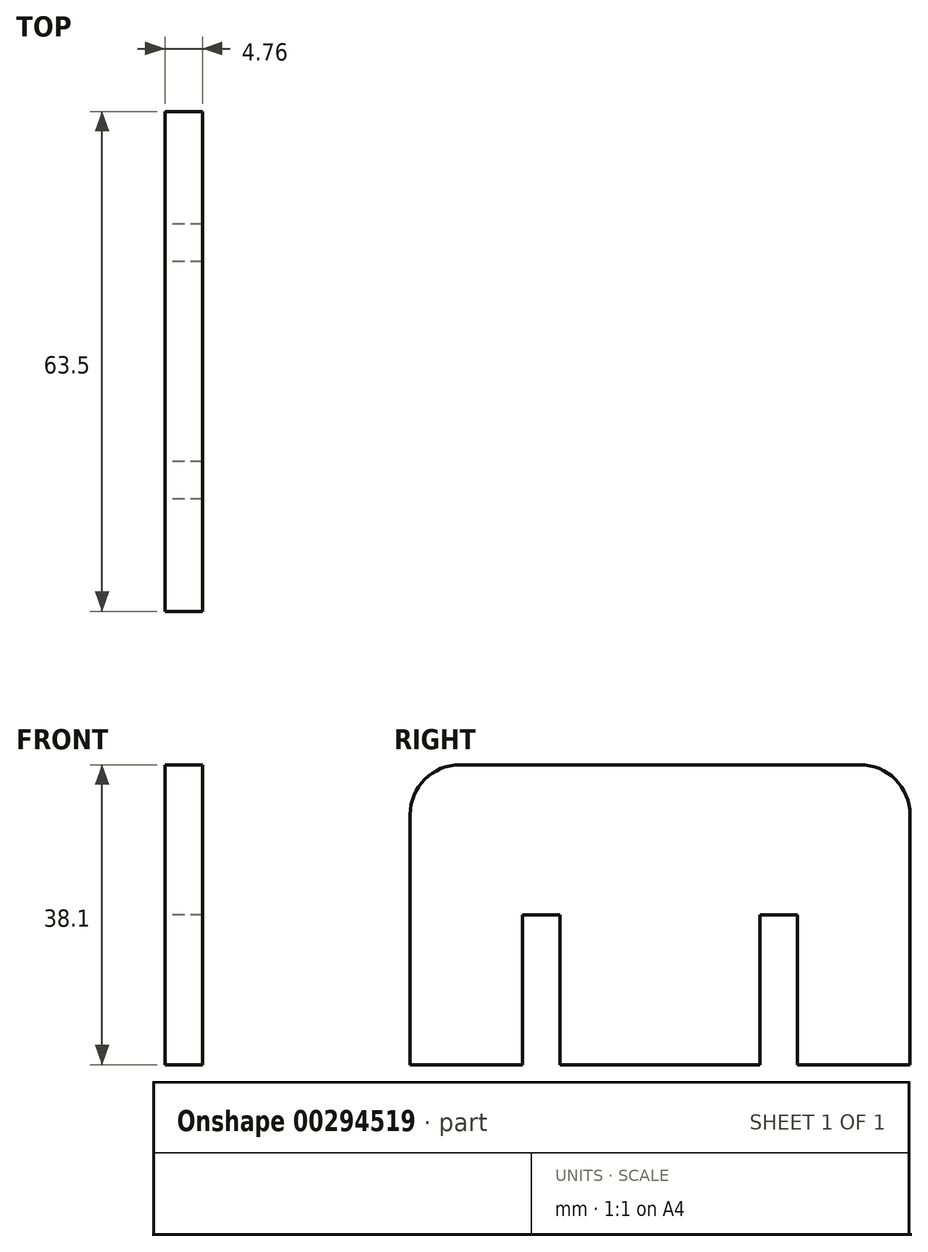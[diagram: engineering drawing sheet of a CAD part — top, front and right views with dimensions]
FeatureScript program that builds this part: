
annotation { "Feature Type Name" : "Feature", "Feature Type Description" : "" }
export const myFeature = defineFeature(function(context is Context, id is Id, definition is map)
    precondition{}
    {
        {
            var Q0;
            Q0=qCreatedBy(makeId("Right.planeOp"),FACE);
            var sketch = newSketch(context, id + "F0", { "sketchPlane" : qUnion([Q0])});
            skLineSegment(sketch, "E0.bottom", {"start": v(0, 0) * mm, "end": v(14.29, 0) * mm});
            skLineSegment(sketch, "E0.top", {"start": v(6.35, 38.1) * mm, "end": v(57.15, 38.1) * mm});
            skLineSegment(sketch, "E0.left", {"start": v(0, 0) * mm, "end": v(0, 31.75) * mm});
            skLineSegment(sketch, "E0.right", {"start": v(63.5, 0) * mm, "end": v(63.5, 31.75) * mm});
            skPoint(sketch, "E1.visualSharp", {"position": v(0, 38.1) * mm});
            skArc(sketch, "E1.filletArc", {"start": v(6.35, 38.1) * mm, "mid": v(1.86, 36.24) * mm, "end": v(0, 31.75) * mm});
            skPoint(sketch, "E2.visualSharp", {"position": v(63.5, 38.1) * mm});
            skArc(sketch, "E2.filletArc", {"start": v(63.5, 31.75) * mm, "mid": v(61.64, 36.24) * mm, "end": v(57.15, 38.1) * mm});
            skLineSegment(sketch, "E3", {"start": v(31.75, 38.1) * mm, "end": v(31.75, 0) * mm, "construction": true});
            skPoint(sketch, "E4.oppositeSnap0", {"position": v(31.75, 19.05) * mm});
            skLineSegment(sketch, "E4.top", {"start": v(44.45, 19.05) * mm, "end": v(49.21, 19.05) * mm});
            skLineSegment(sketch, "E4.left", {"start": v(44.45, 0) * mm, "end": v(44.45, 19.05) * mm});
            skLineSegment(sketch, "E4.right", {"start": v(49.21, 0) * mm, "end": v(49.21, 19.05) * mm});
            skLineSegment(sketch, "E5.MirrorCS", {"start": v(19.05, 19.05) * mm, "end": v(14.29, 19.05) * mm});
            skLineSegment(sketch, "E6.MirrorCS", {"start": v(14.29, 0) * mm, "end": v(14.29, 19.05) * mm});
            skLineSegment(sketch, "E7.MirrorCS", {"start": v(19.05, 0) * mm, "end": v(19.05, 19.05) * mm});
            skLineSegment(sketch, "E8.trimOffspring", {"start": v(19.05, 0) * mm, "end": v(44.45, 0) * mm});
            skLineSegment(sketch, "E9.trimOffspring", {"start": v(49.21, 0) * mm, "end": v(63.5, 0) * mm});
            skSolve(sketch);
        }
        {
            var Q0;
            Q0 = qSketchRegion(id + "F0", true);
            extrude(context, id + "F1", {"entities" : qUnion([Q0]), "depth" : 4.76 * mm});
        }
    });
